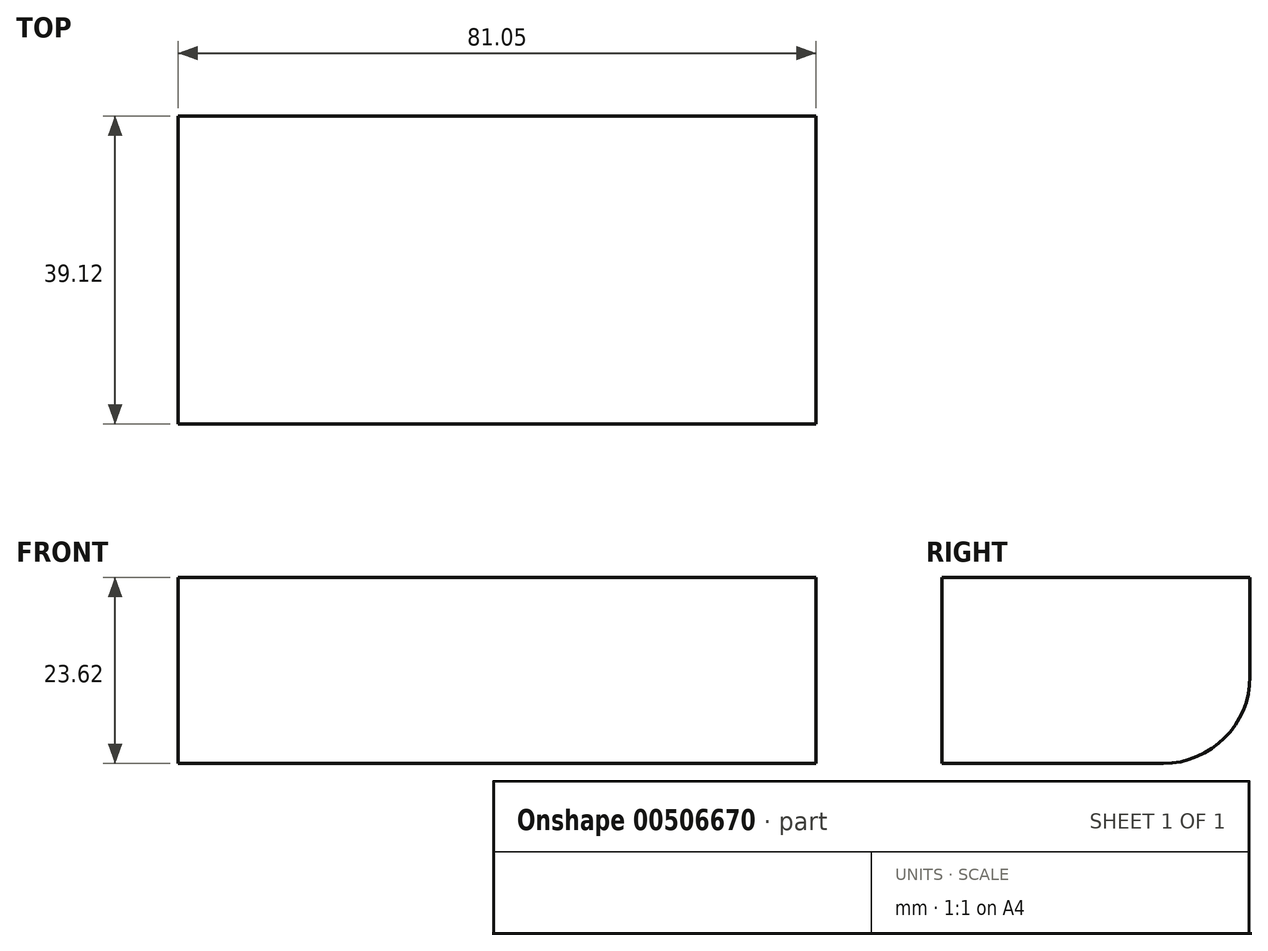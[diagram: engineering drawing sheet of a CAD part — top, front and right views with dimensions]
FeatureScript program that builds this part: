
annotation { "Feature Type Name" : "Feature", "Feature Type Description" : "" }
export const myFeature = defineFeature(function(context is Context, id is Id, definition is map)
    precondition{}
    {
        {
            var Q0;
            Q0=qCreatedBy(makeId("Front.planeOp"),FACE);
            var sketch = newSketch(context, id + "F0", { "sketchPlane" : qUnion([Q0])});
            skLineSegment(sketch, "E0.bottom", {"start": v(-37.7, 12) * mm, "end": v(43.36, 12) * mm});
            skLineSegment(sketch, "E0.top", {"start": v(-37.7, -11.62) * mm, "end": v(43.36, -11.62) * mm});
            skLineSegment(sketch, "E0.left", {"start": v(-37.7, 12) * mm, "end": v(-37.7, -11.62) * mm});
            skLineSegment(sketch, "E0.right", {"start": v(43.36, 12) * mm, "end": v(43.36, -11.62) * mm});
            skSolve(sketch);
        }
        {
            var Q0;
            Q0=makeQuery(id+"F0.imprint","IMPRINT",FACE,{"disambiguationData":[TD([[makeQuery(id+"F0.imprint","IMPRINT",EDGE,{"derivedFrom":sQuery(id+"F0.wireOp",EDGE,"E0.bottom")}),-1.0]])]});
            extrude(context, id + "F1", {"entities" : qUnion([Q0]), "oppositeDirection" : true, "depth" : 39.12 * mm});
        }
        {
            var Q0;
            Q0=makeQuery(id+"F1.opExtrude","CAP_EDGE",EDGE,{"disambiguationData":[OSD([sQuery(id+"F0.wireOp",EDGE,"E0.top")])],"isStart":false});
            fillet(context, id + "F2", {"entities" : qUnion([Q0]), "radius" : 11.04 * mm, "tangentPropagation" : true, "allowEdgeOverflow" : false});
        }
    });
